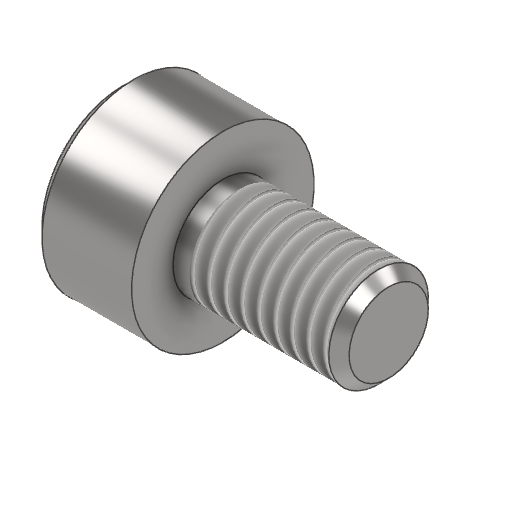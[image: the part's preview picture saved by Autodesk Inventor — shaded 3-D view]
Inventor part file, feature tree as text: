
AUTODESK INVENTOR PART (.ipt)
format: ipt  version: 2023 (Build 270158000, 158)  size: 209,408 bytes
history: native  units: mm
features: other x14, sketch x3, revolve x1, thread x1, hole x1, extrude x1
ambient origin geometry x8: Origin, YZ Plane, XZ Plane, XY Plane, X Axis, Y Axis, Z Axis, Center Point
bodies: Solid1 (feature_tree)
feature tree (21):
  revolve  "Revolution1"  [1 undecoded]
  thread  "Thread1"  [1 undecoded]
  hole  "Hole1"  [1 undecoded]
  extrude  "Extrusion1"  [1 undecoded]
  other  "bolt_XY"
  other  "bolt_YZ"
  other  "bolt_ZX"
  other  "bolt_X"
  other  "bolt_Y"
  other  "bolt_Z"
  other  "bolt_Center"
  other  "nut_XY"
  other  "nut_YZ"
  other  "nut_ZX"
  other  "nut_X"
  other  "nut_Y"
  other  "nut_Z"
  other  "nut_Center"
  sketch  "Sketch_1"  dims[d0=360.0deg d1=4.1935mm d2=0.0mm]
  sketch  "Sketch2"  dims[d3=2.5mm d4=6.0mm d5=4.0mm d6=2.0mm d7=90.0deg d8=1.3mm d9=120.0deg d10=1.3mm d11=0.0mm]
  sketch  "Sketch_3"  dims[d12=0.0mm d13=0.0mm]
note: 4 required parameter values undecoded (feature->parameter linkage not recoverable at this tier; creation-order binding heuristic only, values carry confidence <= 0.55)